# Revit family: rba-bim-rba4613-09 Series
name_source: partatom
category: Plumbing Fixtures
revit_build: Autodesk Revit 2018 (Build: 20170223_1515(x64)
units: mm (PartAtom-declared; Revit-internal decimal feet)

## family parameters
Always vertical = Yes
Cut with Voids When Loaded = No
Part Type = Normal
Room Calculation Point = No
Round Connector Dimension = Use Diameter
Shared = Yes
Work Plane-Based = No

## types (3) — shared parameters
CW Connection = Yes
Description = Leonardo Drop Down Grail Rail
Distance Away from Toilet (default) = 1090 mm  [stored 3.57612 ft]
Distance Away from Wall (default) = 100 mm  [stored 0.328084 ft]
HW Connection = Yes
Manufacturer = RBA Group
Modified Issue = 20200306.01
OFFSET = 1000 mm  [stored 3.28084 ft]
URL = http://www.rba.com.au
Vent Connection = Yes
Waste Connection = Yes

## per-type parameters (varying)
| type | Materials and Finishes |
| RBA4613-091 | Stainless Steel / White Antibacterial Finish |
| RBA4613-098 | Stainless Steel / Matte Black Antibacterial Finish |
| RBA4613-099 | Stainless Steel / Chrome |

note: column(s) folded — value = type name in every type: Model

note: [stored X ft] marks values corroborated as IEEE doubles in the binary element streams (Revit-internal decimal feet)

## geometry (parser evidence)
native form markers: Blend x2, Sweep x2
no freeform markers — native parametric forms only
